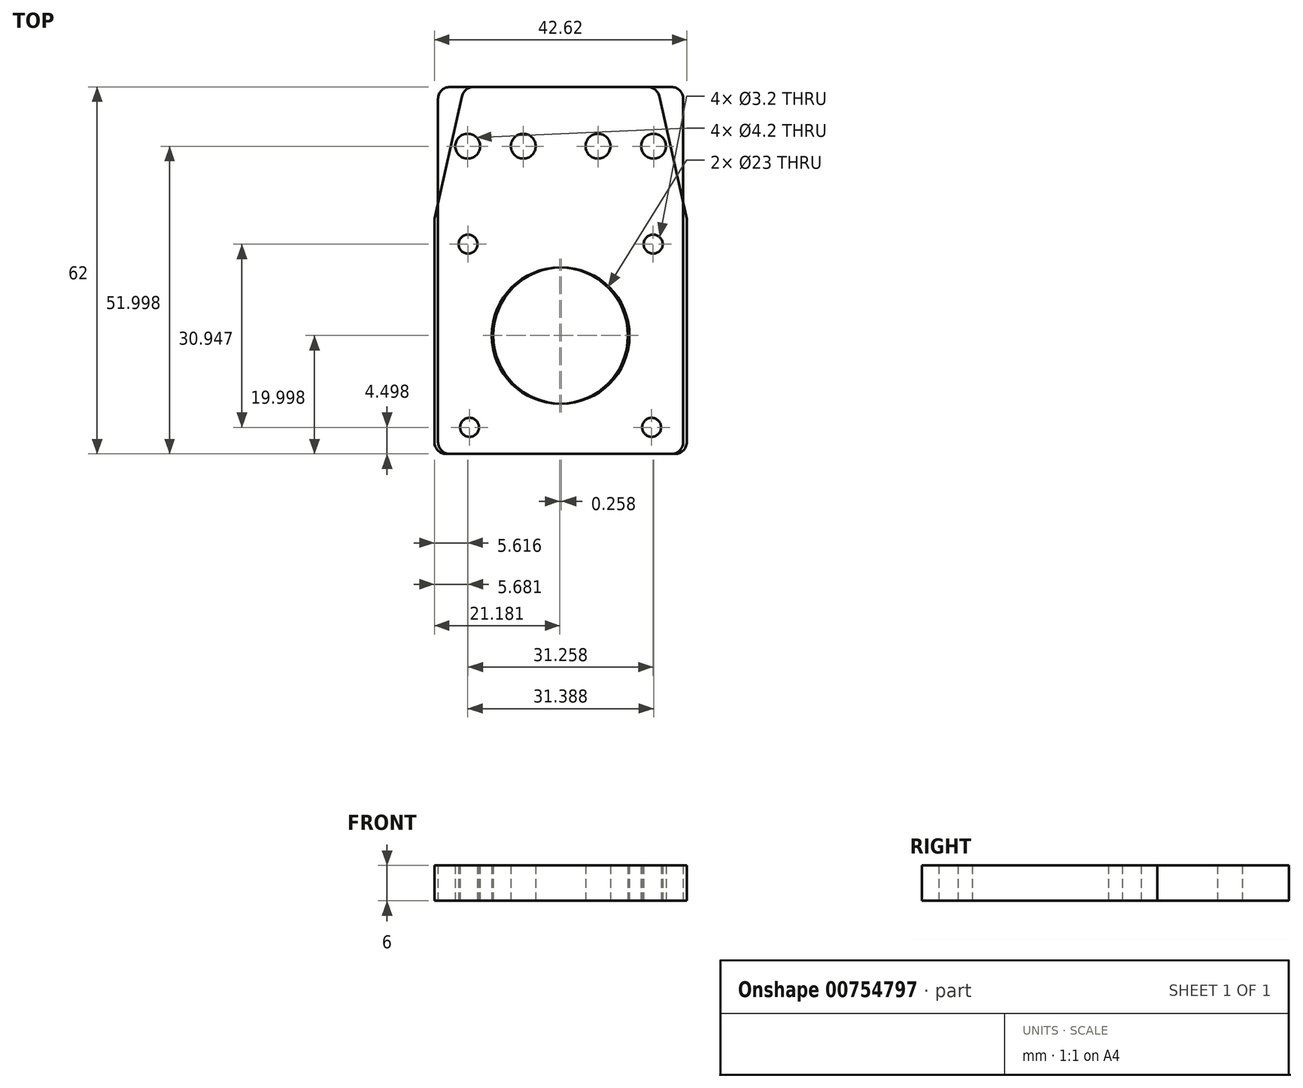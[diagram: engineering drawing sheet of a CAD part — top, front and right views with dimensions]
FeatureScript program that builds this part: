
annotation { "Feature Type Name" : "Feature", "Feature Type Description" : "" }
export const myFeature = defineFeature(function(context is Context, id is Id, definition is map)
    precondition{}
    {
        {
            var Q0;
            Q0=qCreatedBy(makeId("Top.planeOp"),FACE);
            var sketch = newSketch(context, id + "F0", { "sketchPlane" : qUnion([Q0])});
            skCircle(sketch, "E0", {"center": v(-0.13, -28.42) * mm, "radius": 11.5 * mm});
            skCircle(sketch, "E1", {"center": v(15.37, -43.92) * mm, "radius": 1.6 * mm});
            skCircle(sketch, "E2", {"center": v(-15.63, -12.97) * mm, "radius": 1.6 * mm});
            skLineSegment(sketch, "E3.bottom", {"start": v(-18.7, 13.58) * mm, "end": v(14.7, 13.58) * mm});
            skLineSegment(sketch, "E3.top", {"start": v(-18.7, -48.42) * mm, "end": v(19.3, -48.42) * mm});
            skLineSegment(sketch, "E3.left", {"start": v(-20.7, 11.58) * mm, "end": v(-20.7, -46.42) * mm});
            skLineSegment(sketch, "E3.right", {"start": v(21.3, -8.68) * mm, "end": v(21.3, -46.42) * mm});
            skCircle(sketch, "E4", {"center": v(-15.7, 3.58) * mm, "radius": 2.1 * mm});
            skCircle(sketch, "E5", {"center": v(6.3, 3.58) * mm, "radius": 2.1 * mm});
            skPoint(sketch, "E6.visualSharp", {"position": v(-20.7, 13.58) * mm});
            skArc(sketch, "E6.filletArc", {"start": v(-18.7, 13.58) * mm, "mid": v(-20.1, 13) * mm, "end": v(-20.7, 11.58) * mm});
            skPoint(sketch, "E7.visualSharp", {"position": v(21.3, -48.42) * mm});
            skArc(sketch, "E7.filletArc", {"start": v(19.3, -48.42) * mm, "mid": v(20.72, -47.84) * mm, "end": v(21.3, -46.42) * mm});
            skPoint(sketch, "E8.visualSharp", {"position": v(-20.7, -48.42) * mm});
            skArc(sketch, "E8.filletArc", {"start": v(-20.7, -46.42) * mm, "mid": v(-20.1, -47.84) * mm, "end": v(-18.7, -48.42) * mm});
            skLineSegment(sketch, "E9", {"start": v(16.66, 12.02) * mm, "end": v(21.3, -8.68) * mm});
            skPoint(sketch, "E10.visualSharp", {"position": v(16.3, 13.58) * mm});
            skArc(sketch, "E10.filletArc", {"start": v(16.66, 12.02) * mm, "mid": v(15.96, 13.14) * mm, "end": v(14.7, 13.58) * mm});
            skSolve(sketch);
        }
        {
            var Q0;
            Q0=qSketchRegion(id+"F0",true);
            extrude(context, id + "F1", {"entities" : qUnion([Q0]), "offsetDistance" : 25 * mm, "depth" : 6 * mm});
        }
        {
            var Q0;
            Q0=makeQuery(id+"F1.opExtrude","SWEPT_BODY",BODY,{"disambiguationData":[OSD([sQuery(id+"F0.wireOp",EDGE,"E0"),sQuery(id+"F0.wireOp",EDGE,"E1"),sQuery(id+"F0.wireOp",EDGE,"E2"),sQuery(id+"F0.wireOp",EDGE,"E3.bottom"),sQuery(id+"F0.wireOp",EDGE,"E3.top"),sQuery(id+"F0.wireOp",EDGE,"E3.left"),sQuery(id+"F0.wireOp",EDGE,"E3.right"),sQuery(id+"F0.wireOp",EDGE,"E4"),sQuery(id+"F0.wireOp",EDGE,"E5"),sQuery(id+"F0.wireOp",EDGE,"E6.filletArc"),sQuery(id+"F0.wireOp",EDGE,"E7.filletArc"),sQuery(id+"F0.wireOp",EDGE,"E8.filletArc"),sQuery(id+"F0.wireOp",EDGE,"E9")])]});
            var Q1;
            Q1=qCreatedBy(makeId("Right.planeOp"),FACE);
            mirror(context, id + "F2", {"entities" : qUnion([Q0]), "mirrorPlane" : qUnion([Q1])});
        }
    });
